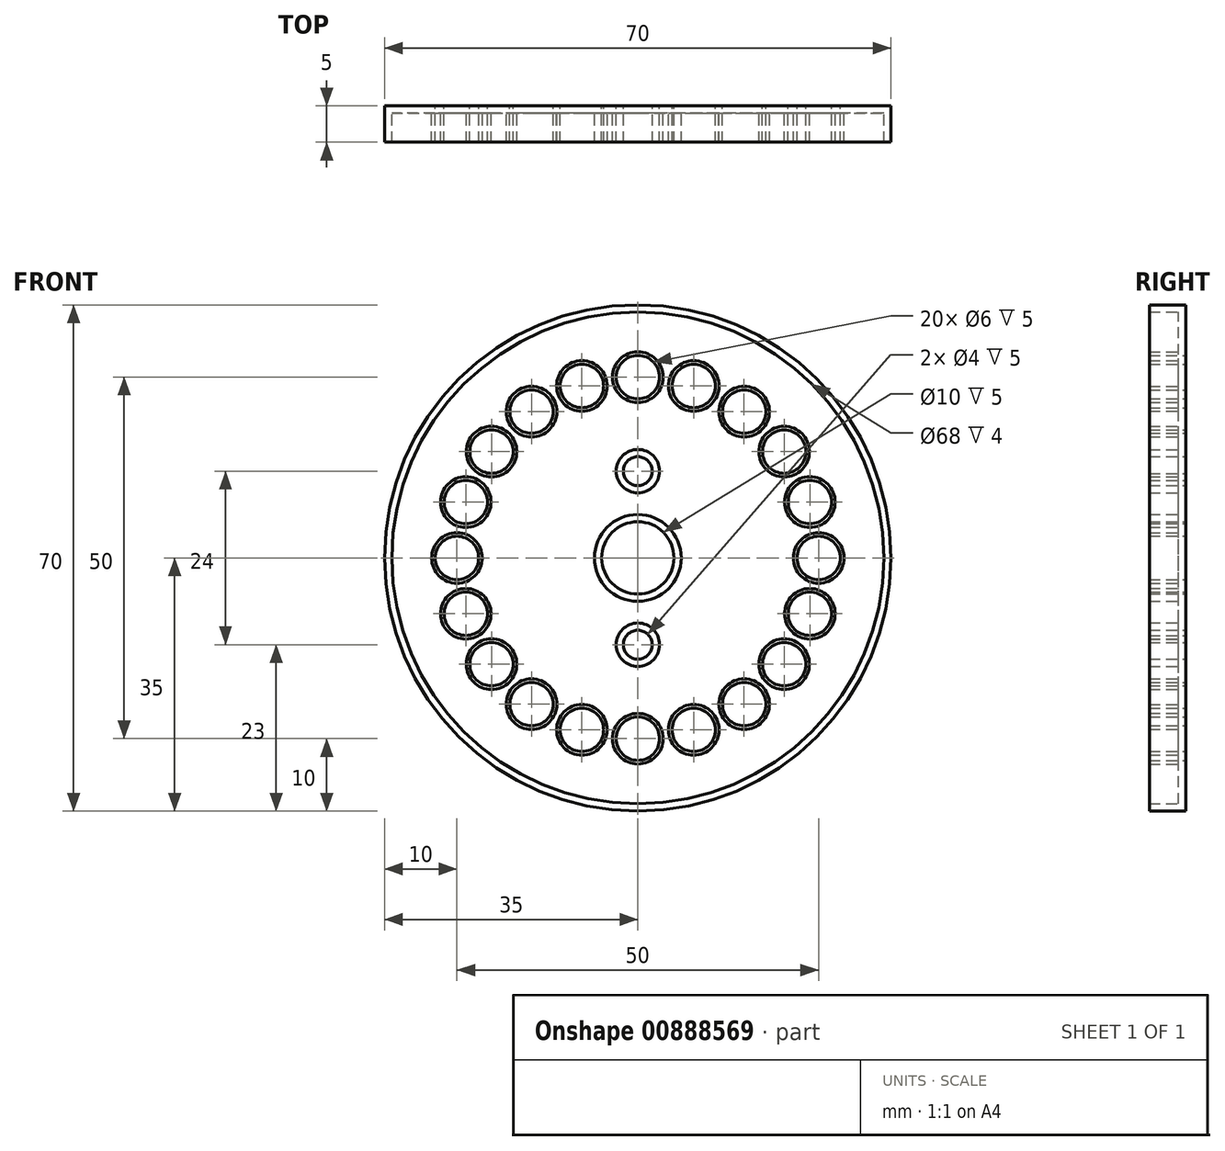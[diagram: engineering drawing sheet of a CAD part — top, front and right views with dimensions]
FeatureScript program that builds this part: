
annotation { "Feature Type Name" : "Feature", "Feature Type Description" : "" }
export const myFeature = defineFeature(function(context is Context, id is Id, definition is map)
    precondition{}
    {
        {
            var Q0;
            Q0=qCreatedBy(makeId("Front.planeOp"),FACE);
            var sketch = newSketch(context, id + "F0", { "sketchPlane" : qUnion([Q0])});
            skCircle(sketch, "E0", {"center": v(0, 0) * mm, "radius": 35 * mm});
            skCircle(sketch, "E1", {"center": v(0, 25) * mm, "radius": 3 * mm});
            skCircle(sketch, "E2.1.0", {"center": v(-7.73, 23.78) * mm, "radius": 3 * mm});
            skCircle(sketch, "E2.2.0", {"center": v(-14.7, 20.23) * mm, "radius": 3 * mm});
            skCircle(sketch, "E2.3.0", {"center": v(-20.23, 14.7) * mm, "radius": 3 * mm});
            skCircle(sketch, "E2.4.0", {"center": v(-23.78, 7.73) * mm, "radius": 3 * mm});
            skCircle(sketch, "E2.5.0", {"center": v(-25, 0) * mm, "radius": 3 * mm});
            skCircle(sketch, "E2.6.0", {"center": v(-23.78, -7.73) * mm, "radius": 3 * mm});
            skCircle(sketch, "E2.7.0", {"center": v(-20.23, -14.7) * mm, "radius": 3 * mm});
            skCircle(sketch, "E2.8.0", {"center": v(-14.7, -20.23) * mm, "radius": 3 * mm});
            skCircle(sketch, "E2.9.0", {"center": v(-7.73, -23.78) * mm, "radius": 3 * mm});
            skCircle(sketch, "E2.10.0", {"center": v(0, -25) * mm, "radius": 3 * mm});
            skCircle(sketch, "E2.11.0", {"center": v(7.73, -23.78) * mm, "radius": 3 * mm});
            skCircle(sketch, "E2.12.0", {"center": v(14.7, -20.23) * mm, "radius": 3 * mm});
            skCircle(sketch, "E2.13.0", {"center": v(20.23, -14.7) * mm, "radius": 3 * mm});
            skCircle(sketch, "E2.14.0", {"center": v(23.78, -7.73) * mm, "radius": 3 * mm});
            skCircle(sketch, "E2.15.0", {"center": v(25, 0) * mm, "radius": 3 * mm});
            skCircle(sketch, "E2.16.0", {"center": v(23.78, 7.73) * mm, "radius": 3 * mm});
            skCircle(sketch, "E2.17.0", {"center": v(20.23, 14.7) * mm, "radius": 3 * mm});
            skCircle(sketch, "E2.18.0", {"center": v(14.7, 20.23) * mm, "radius": 3 * mm});
            skCircle(sketch, "E2.19.0", {"center": v(7.73, 23.78) * mm, "radius": 3 * mm});
            skCircle(sketch, "E3", {"center": v(0, 12) * mm, "radius": 2 * mm});
            skCircle(sketch, "E4.MirrorC", {"center": v(0, -12) * mm, "radius": 2 * mm});
            skCircle(sketch, "E5", {"center": v(0, 0) * mm, "radius": 5 * mm});
            skSolve(sketch);
        }
        {
            var Q0;
            Q0 = qSketchRegion(id + "F0", true);
            extrude(context, id + "F1", {"entities" : qUnion([Q0]), "depth" : 1 * mm, "offsetDistance" : 25 * mm});
        }
        {
            var Q0;
            Q0=makeQuery(id+"F1.opExtrude","CAP_FACE",FACE,{"disambiguationData":[OSD([sQuery(id+"F0.wireOp",EDGE,"E0"),sQuery(id+"F0.wireOp",EDGE,"E1"),sQuery(id+"F0.wireOp",EDGE,"E2.1.0"),sQuery(id+"F0.wireOp",EDGE,"E2.2.0"),sQuery(id+"F0.wireOp",EDGE,"E2.3.0"),sQuery(id+"F0.wireOp",EDGE,"E2.4.0"),sQuery(id+"F0.wireOp",EDGE,"E2.5.0"),sQuery(id+"F0.wireOp",EDGE,"E2.6.0"),sQuery(id+"F0.wireOp",EDGE,"E2.7.0"),sQuery(id+"F0.wireOp",EDGE,"E2.8.0"),sQuery(id+"F0.wireOp",EDGE,"E2.9.0"),sQuery(id+"F0.wireOp",EDGE,"E2.10.0"),sQuery(id+"F0.wireOp",EDGE,"E2.11.0"),sQuery(id+"F0.wireOp",EDGE,"E2.12.0"),sQuery(id+"F0.wireOp",EDGE,"E2.13.0"),sQuery(id+"F0.wireOp",EDGE,"E2.14.0"),sQuery(id+"F0.wireOp",EDGE,"E2.15.0"),sQuery(id+"F0.wireOp",EDGE,"E2.16.0"),sQuery(id+"F0.wireOp",EDGE,"E2.17.0"),sQuery(id+"F0.wireOp",EDGE,"E2.18.0"),sQuery(id+"F0.wireOp",EDGE,"E2.19.0"),sQuery(id+"F0.wireOp",EDGE,"E3"),sQuery(id+"F0.wireOp",EDGE,"E4.MirrorC"),sQuery(id+"F0.wireOp",EDGE,"E5")])],"isStart":false});
            var sketch = newSketch(context, id + "F2", { "sketchPlane" : qUnion([Q0])});
            skCircle(sketch, "E6.0", {"center": v(0, 25) * mm, "radius": 3 * mm});
            skCircle(sketch, "E7.0", {"center": v(0, 25) * mm, "radius": 3.5 * mm});
            skCircle(sketch, "E8.1.0", {"center": v(-7.73, 23.78) * mm, "radius": 3 * mm});
            skCircle(sketch, "E8.1.1", {"center": v(-7.73, 23.78) * mm, "radius": 3.5 * mm});
            skCircle(sketch, "E8.2.0", {"center": v(-14.7, 20.23) * mm, "radius": 3 * mm});
            skCircle(sketch, "E8.2.1", {"center": v(-14.7, 20.23) * mm, "radius": 3.5 * mm});
            skCircle(sketch, "E8.3.0", {"center": v(-20.23, 14.7) * mm, "radius": 3 * mm});
            skCircle(sketch, "E8.3.1", {"center": v(-20.23, 14.7) * mm, "radius": 3.5 * mm});
            skCircle(sketch, "E8.4.0", {"center": v(-23.78, 7.73) * mm, "radius": 3 * mm});
            skCircle(sketch, "E8.4.1", {"center": v(-23.78, 7.73) * mm, "radius": 3.5 * mm});
            skCircle(sketch, "E8.5.0", {"center": v(-25, 0) * mm, "radius": 3 * mm});
            skCircle(sketch, "E8.5.1", {"center": v(-25, 0) * mm, "radius": 3.5 * mm});
            skCircle(sketch, "E8.6.0", {"center": v(-23.78, -7.73) * mm, "radius": 3 * mm});
            skCircle(sketch, "E8.6.1", {"center": v(-23.78, -7.73) * mm, "radius": 3.5 * mm});
            skCircle(sketch, "E8.7.0", {"center": v(-20.23, -14.7) * mm, "radius": 3 * mm});
            skCircle(sketch, "E8.7.1", {"center": v(-20.23, -14.7) * mm, "radius": 3.5 * mm});
            skCircle(sketch, "E8.8.0", {"center": v(-14.7, -20.23) * mm, "radius": 3 * mm});
            skCircle(sketch, "E8.8.1", {"center": v(-14.7, -20.23) * mm, "radius": 3.5 * mm});
            skCircle(sketch, "E8.9.0", {"center": v(-7.73, -23.78) * mm, "radius": 3 * mm});
            skCircle(sketch, "E8.9.1", {"center": v(-7.73, -23.78) * mm, "radius": 3.5 * mm});
            skCircle(sketch, "E8.10.0", {"center": v(0, -25) * mm, "radius": 3 * mm});
            skCircle(sketch, "E8.10.1", {"center": v(0, -25) * mm, "radius": 3.5 * mm});
            skCircle(sketch, "E8.11.0", {"center": v(7.73, -23.78) * mm, "radius": 3 * mm});
            skCircle(sketch, "E8.11.1", {"center": v(7.73, -23.78) * mm, "radius": 3.5 * mm});
            skCircle(sketch, "E8.12.0", {"center": v(14.7, -20.23) * mm, "radius": 3 * mm});
            skCircle(sketch, "E8.12.1", {"center": v(14.7, -20.23) * mm, "radius": 3.5 * mm});
            skCircle(sketch, "E8.13.0", {"center": v(20.23, -14.7) * mm, "radius": 3 * mm});
            skCircle(sketch, "E8.13.1", {"center": v(20.23, -14.7) * mm, "radius": 3.5 * mm});
            skCircle(sketch, "E8.14.0", {"center": v(23.78, -7.73) * mm, "radius": 3 * mm});
            skCircle(sketch, "E8.14.1", {"center": v(23.78, -7.73) * mm, "radius": 3.5 * mm});
            skCircle(sketch, "E8.15.0", {"center": v(25, 0) * mm, "radius": 3 * mm});
            skCircle(sketch, "E8.15.1", {"center": v(25, 0) * mm, "radius": 3.5 * mm});
            skCircle(sketch, "E8.16.0", {"center": v(23.78, 7.73) * mm, "radius": 3 * mm});
            skCircle(sketch, "E8.16.1", {"center": v(23.78, 7.73) * mm, "radius": 3.5 * mm});
            skCircle(sketch, "E8.17.0", {"center": v(20.23, 14.7) * mm, "radius": 3 * mm});
            skCircle(sketch, "E8.17.1", {"center": v(20.23, 14.7) * mm, "radius": 3.5 * mm});
            skCircle(sketch, "E8.18.0", {"center": v(14.7, 20.23) * mm, "radius": 3 * mm});
            skCircle(sketch, "E8.18.1", {"center": v(14.7, 20.23) * mm, "radius": 3.5 * mm});
            skCircle(sketch, "E8.19.0", {"center": v(7.73, 23.78) * mm, "radius": 3 * mm});
            skCircle(sketch, "E8.19.1", {"center": v(7.73, 23.78) * mm, "radius": 3.5 * mm});
            skPoint(sketch, "E8.center", {"position": v(0, 0) * mm});
            skCircle(sketch, "E9.1", {"center": v(0, 0) * mm, "radius": 35 * mm});
            skCircle(sketch, "E10.0", {"center": v(0, 0) * mm, "radius": 34 * mm});
            skCircle(sketch, "E11.0", {"center": v(0, -12) * mm, "radius": 3 * mm});
            skCircle(sketch, "E12.0", {"center": v(0, 0) * mm, "radius": 6 * mm});
            skCircle(sketch, "E13.0", {"center": v(0, 12) * mm, "radius": 3 * mm});
            skCircle(sketch, "E14.0", {"center": v(0, 12) * mm, "radius": 2 * mm});
            skCircle(sketch, "E15.0", {"center": v(0, 0) * mm, "radius": 5 * mm});
            skCircle(sketch, "E16.0", {"center": v(0, -12) * mm, "radius": 2 * mm});
            skSolve(sketch);
        }
        {
            var Q0;
            Q0 = qSketchRegion(id + "F2", true);
            var Q1;
            Q1=makeQuery(id+"F2.imprint","IMPRINT",FACE,{"disambiguationData":[TD([[makeQuery(id+"F2.imprint","IMPRINT",EDGE,{"derivedFrom":sQuery(id+"F2.wireOp",EDGE,"E13.0")}),1.0]])]});
            var Q2;
            Q2=makeQuery(id+"F2.imprint","IMPRINT",FACE,{"disambiguationData":[TD([[makeQuery(id+"F2.imprint","IMPRINT",EDGE,{"derivedFrom":sQuery(id+"F2.wireOp",EDGE,"E12.0")}),1.0]])]});
            var Q3;
            Q3=makeQuery(id+"F2.imprint","IMPRINT",FACE,{"disambiguationData":[TD([[makeQuery(id+"F2.imprint","IMPRINT",EDGE,{"derivedFrom":sQuery(id+"F2.wireOp",EDGE,"E11.0")}),1.0]])]});
            var Q4;
            Q4=makeQuery(id+"F2.imprint","IMPRINT",FACE,{"disambiguationData":[TD([[makeQuery(id+"F2.imprint","IMPRINT",EDGE,{"derivedFrom":sQuery(id+"F2.wireOp",EDGE,"E8.2.0")}),-1.0]])]});
            var Q5;
            Q5=makeQuery(id+"F2.imprint","IMPRINT",FACE,{"disambiguationData":[TD([[makeQuery(id+"F2.imprint","IMPRINT",EDGE,{"derivedFrom":sQuery(id+"F2.wireOp",EDGE,"E8.3.0")}),-1.0]])]});
            var Q6;
            Q6=makeQuery(id+"F2.imprint","IMPRINT",FACE,{"disambiguationData":[TD([[makeQuery(id+"F2.imprint","IMPRINT",EDGE,{"derivedFrom":sQuery(id+"F2.wireOp",EDGE,"E8.4.0")}),-1.0]])]});
            var Q7;
            Q7=makeQuery(id+"F2.imprint","IMPRINT",FACE,{"disambiguationData":[TD([[makeQuery(id+"F2.imprint","IMPRINT",EDGE,{"derivedFrom":sQuery(id+"F2.wireOp",EDGE,"E8.5.0")}),-1.0]])]});
            var Q8;
            Q8=makeQuery(id+"F2.imprint","IMPRINT",FACE,{"disambiguationData":[TD([[makeQuery(id+"F2.imprint","IMPRINT",EDGE,{"derivedFrom":sQuery(id+"F2.wireOp",EDGE,"E8.6.0")}),-1.0]])]});
            var Q9;
            Q9=makeQuery(id+"F2.imprint","IMPRINT",FACE,{"disambiguationData":[TD([[makeQuery(id+"F2.imprint","IMPRINT",EDGE,{"derivedFrom":sQuery(id+"F2.wireOp",EDGE,"E8.7.0")}),-1.0]])]});
            var Q10;
            Q10=makeQuery(id+"F2.imprint","IMPRINT",FACE,{"disambiguationData":[TD([[makeQuery(id+"F2.imprint","IMPRINT",EDGE,{"derivedFrom":sQuery(id+"F2.wireOp",EDGE,"E8.8.0")}),-1.0]])]});
            var Q11;
            Q11=makeQuery(id+"F2.imprint","IMPRINT",FACE,{"disambiguationData":[TD([[makeQuery(id+"F2.imprint","IMPRINT",EDGE,{"derivedFrom":sQuery(id+"F2.wireOp",EDGE,"E8.9.0")}),-1.0]])]});
            var Q12;
            Q12=makeQuery(id+"F2.imprint","IMPRINT",FACE,{"disambiguationData":[TD([[makeQuery(id+"F2.imprint","IMPRINT",EDGE,{"derivedFrom":sQuery(id+"F2.wireOp",EDGE,"E8.10.0")}),-1.0]])]});
            var Q13;
            Q13=makeQuery(id+"F2.imprint","IMPRINT",FACE,{"disambiguationData":[TD([[makeQuery(id+"F2.imprint","IMPRINT",EDGE,{"derivedFrom":sQuery(id+"F2.wireOp",EDGE,"E8.11.0")}),-1.0]])]});
            var Q14;
            Q14=makeQuery(id+"F2.imprint","IMPRINT",FACE,{"disambiguationData":[TD([[makeQuery(id+"F2.imprint","IMPRINT",EDGE,{"derivedFrom":sQuery(id+"F2.wireOp",EDGE,"E8.12.0")}),-1.0]])]});
            var Q15;
            Q15=makeQuery(id+"F2.imprint","IMPRINT",FACE,{"disambiguationData":[TD([[makeQuery(id+"F2.imprint","IMPRINT",EDGE,{"derivedFrom":sQuery(id+"F2.wireOp",EDGE,"E8.13.0")}),-1.0]])]});
            var Q16;
            Q16=makeQuery(id+"F2.imprint","IMPRINT",FACE,{"disambiguationData":[TD([[makeQuery(id+"F2.imprint","IMPRINT",EDGE,{"derivedFrom":sQuery(id+"F2.wireOp",EDGE,"E8.14.0")}),-1.0]])]});
            var Q17;
            Q17=makeQuery(id+"F2.imprint","IMPRINT",FACE,{"disambiguationData":[TD([[makeQuery(id+"F2.imprint","IMPRINT",EDGE,{"derivedFrom":sQuery(id+"F2.wireOp",EDGE,"E8.15.0")}),-1.0]])]});
            var Q18;
            Q18=makeQuery(id+"F2.imprint","IMPRINT",FACE,{"disambiguationData":[TD([[makeQuery(id+"F2.imprint","IMPRINT",EDGE,{"derivedFrom":sQuery(id+"F2.wireOp",EDGE,"E8.16.0")}),-1.0]])]});
            var Q19;
            Q19=makeQuery(id+"F2.imprint","IMPRINT",FACE,{"disambiguationData":[TD([[makeQuery(id+"F2.imprint","IMPRINT",EDGE,{"derivedFrom":sQuery(id+"F2.wireOp",EDGE,"E8.17.0")}),-1.0]])]});
            var Q20;
            Q20=makeQuery(id+"F2.imprint","IMPRINT",FACE,{"disambiguationData":[TD([[makeQuery(id+"F2.imprint","IMPRINT",EDGE,{"derivedFrom":sQuery(id+"F2.wireOp",EDGE,"E8.18.0")}),-1.0]])]});
            var Q21;
            Q21=makeQuery(id+"F2.imprint","IMPRINT",FACE,{"disambiguationData":[TD([[makeQuery(id+"F2.imprint","IMPRINT",EDGE,{"derivedFrom":sQuery(id+"F2.wireOp",EDGE,"E8.19.0")}),-1.0]])]});
            var Q22;
            Q22=makeQuery(id+"F2.imprint","IMPRINT",FACE,{"disambiguationData":[TD([[makeQuery(id+"F2.imprint","IMPRINT",EDGE,{"derivedFrom":sQuery(id+"F2.wireOp",EDGE,"E8.1.0")}),-1.0]])]});
            var Q23;
            Q23=makeQuery(id+"F2.imprint","IMPRINT",FACE,{"disambiguationData":[TD([[makeQuery(id+"F2.imprint","IMPRINT",EDGE,{"derivedFrom":sQuery(id+"F2.wireOp",EDGE,"E6.0")}),-1.0]])]});
            extrude(context, id + "F3", {"entities" : qUnion([Q0, Q1, Q2, Q3, Q4, Q5, Q6, Q7, Q8, Q9, Q10, Q11, Q12, Q13, Q14, Q15, Q16, Q17, Q18, Q19, Q20, Q21, Q22, Q23]), "operationType" : NewBodyOperationType.ADD, "depth" : 4 * mm, "offsetDistance" : 25 * mm});
        }
    });
